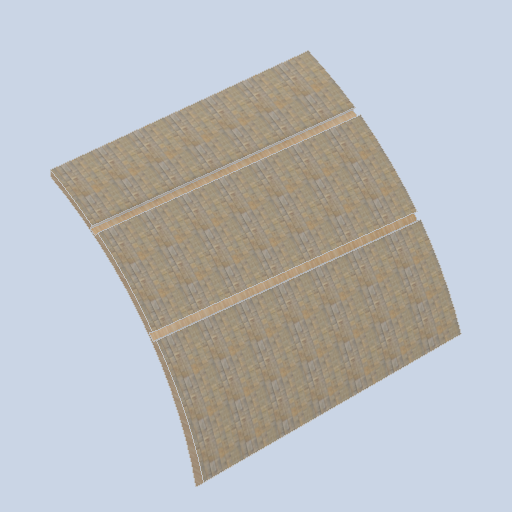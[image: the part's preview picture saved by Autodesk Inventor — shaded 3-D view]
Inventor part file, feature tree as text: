
AUTODESK INVENTOR PART (.ipt)
format: ipt  version: 2024.2 (Build 282272000, 272)  size: 342,528 bytes
history: native  units: in
note: dims shown in document units (in); Inventor stores cm internally (conversion verified against a paired STEP export)
features: other x3, sketch x2, plane x2
ambient origin geometry x8: Origin, YZ Plane, XZ Plane, XY Plane, X Axis, Y Axis, Z Axis, Center Point
bodies: Solid1 (feature_tree)
feature tree (7):
  other  "panel_block_02.ipt"
  other  "Solid1::panel_block_02.ipt"
  other  "TaggingFeature1"
  sketch  "Sketch1"  dims[d0=0.3937in]
  sketch  "Sketch2"
  plane  "Work Plane1"
  plane  "Work Plane2"
